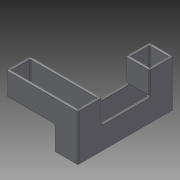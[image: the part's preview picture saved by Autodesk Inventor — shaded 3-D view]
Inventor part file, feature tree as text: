
AUTODESK INVENTOR PART (.ipt)
format: ipt  version: 2014 (Build 180170000, 170)  size: 233,984 bytes
history: native  units: in
note: dims shown in document units (in); Inventor stores cm internally (conversion verified against a paired STEP export)
features: plane x8, extrude x3, other x1, shell x1, fillet x1, sketch x1
ambient origin geometry x8: Origin, YZ Plane, XZ Plane, XY Plane, X Axis, Y Axis, Z Axis, Center Point
bodies: Solid1 (feature_tree)
feature tree (15):
  other  "Cube Master.ipt"
  extrude  "Extrusion1"  Depth=0.3937in
  extrude  "Extrusion2"  Depth=0.0193in TaperAngle=0.0deg
  extrude  "Extrusion3"  Depth=0.0193in TaperAngle=0.0deg
  shell  "Shell1"  Thickness=1.0in
  fillet  "Fillet1"  Radius=0.0394in
  sketch  "Sketch1"  dims[d0=0.3937in d1=0.3937in d2=1.0in d3=0.0in d4=1.0in d5=0.0in d6=1.0in d7=0.0in d8=0.0394in d9=0.0193in d10=0.0193in]
  plane  "Work Plane1"
  plane  "Work Plane2"
  plane  "Work Plane3"
  plane  "Work Plane4"
  plane  "Work Plane5"
  plane  "Work Plane6"
  plane  "Work Plane7"
  plane  "Work Plane8"
